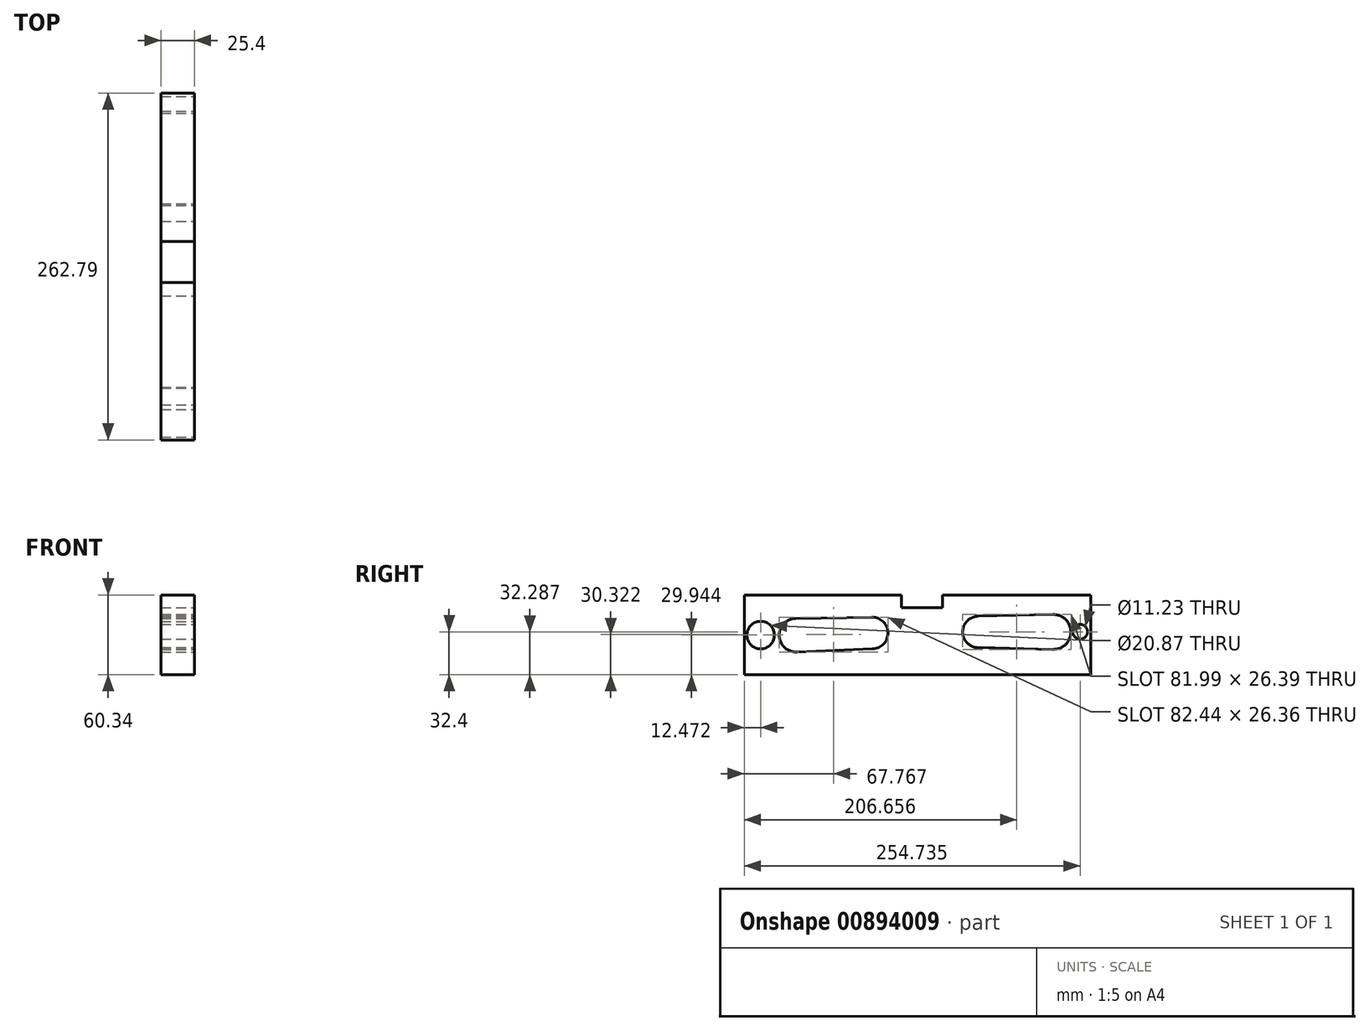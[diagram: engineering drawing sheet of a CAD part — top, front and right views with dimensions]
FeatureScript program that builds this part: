
annotation { "Feature Type Name" : "Feature", "Feature Type Description" : "" }
export const myFeature = defineFeature(function(context is Context, id is Id, definition is map)
    precondition{}
    {
        {
            var Q0;
            Q0=qCreatedBy(makeId("Right.planeOp"),FACE);
            var sketch = newSketch(context, id + "F0", { "sketchPlane" : qUnion([Q0])});
            skLineSegment(sketch, "E0", {"start": v(-89.26, -13.23) * mm, "end": v(-89.26, -73.57) * mm});
            skLineSegment(sketch, "E1", {"start": v(-89.26, -73.57) * mm, "end": v(173.53, -73.57) * mm});
            skLineSegment(sketch, "E2", {"start": v(173.53, -73.57) * mm, "end": v(173.53, -13.23) * mm});
            skLineSegment(sketch, "E3", {"start": v(173.53, -13.23) * mm, "end": v(-89.26, -13.23) * mm});
            skSolve(sketch);
        }
        {
            var Q0;
            Q0 = qSketchRegion(id + "F0", true);
            extrude(context, id + "F1", {"entities" : qUnion([Q0]), "depth" : 25.4 * mm, "offsetDistance" : 25.4 * mm});
        }
        {
            var Q0;
            Q0=makeQuery(id+"F1.opExtrude","CAP_FACE",FACE,{"disambiguationData":[OSD([sQuery(id+"F0.wireOp",EDGE,"E0"),sQuery(id+"F0.wireOp",EDGE,"E1"),sQuery(id+"F0.wireOp",EDGE,"E2"),sQuery(id+"F0.wireOp",EDGE,"E3")])],"isStart":false});
            var sketch = newSketch(context, id + "F2", { "sketchPlane" : qUnion([Q0])});
            skArc(sketch, "E4", {"start": v(-50, -31.03) * mm, "mid": v(-62.71, -44.12) * mm, "end": v(-49.24, -56.43) * mm});
            skArc(sketch, "E5", {"start": v(8.18, -54.13) * mm, "mid": v(19.73, -41.76) * mm, "end": v(7.5, -30.07) * mm});
            skArc(sketch, "E6", {"start": v(88.31, -29.35) * mm, "mid": v(76.4, -41.92) * mm, "end": v(89.6, -53.14) * mm});
            skArc(sketch, "E7", {"start": v(144.88, -54.48) * mm, "mid": v(158.4, -41.3) * mm, "end": v(144.9, -28.09) * mm});
            skLineSegment(sketch, "E8", {"start": v(-50, -31.03) * mm, "end": v(7.5, -30.07) * mm});
            skLineSegment(sketch, "E9", {"start": v(-49.24, -56.43) * mm, "end": v(8.18, -54.13) * mm});
            skLineSegment(sketch, "E10", {"start": v(89.6, -53.14) * mm, "end": v(144.88, -54.48) * mm});
            skLineSegment(sketch, "E11", {"start": v(88.31, -29.35) * mm, "end": v(144.9, -28.09) * mm});
            skSolve(sketch);
        }
        {
            var Q0;
            Q0 = qSketchRegion(id + "F2", true);
            extrude(context, id + "F3", {"entities" : qUnion([Q0]), "operationType" : NewBodyOperationType.REMOVE, "oppositeDirection" : true, "depth" : 25.4 * mm, "offsetDistance" : 25.4 * mm});
        }
        {
            var Q0;
            Q0=makeQuery(id+"F1.opExtrude","CAP_FACE",FACE,{"disambiguationData":[OSD([sQuery(id+"F0.wireOp",EDGE,"E0"),sQuery(id+"F0.wireOp",EDGE,"E1"),sQuery(id+"F0.wireOp",EDGE,"E2"),sQuery(id+"F0.wireOp",EDGE,"E3")])],"isStart":false});
            var sketch = newSketch(context, id + "F4", { "sketchPlane" : qUnion([Q0])});
            skLineSegment(sketch, "E12", {"start": v(30.1, -13.23) * mm, "end": v(30.1, -22.8) * mm});
            skLineSegment(sketch, "E13", {"start": v(30.1, -22.8) * mm, "end": v(61.07, -22.8) * mm});
            skLineSegment(sketch, "E14", {"start": v(61.07, -22.8) * mm, "end": v(61.07, -13.23) * mm});
            skLineSegment(sketch, "E15", {"start": v(30.1, -13.23) * mm, "end": v(61.07, -13.23) * mm});
            skSolve(sketch);
        }
        {
            var Q0;
            Q0 = qSketchRegion(id + "F4", true);
            extrude(context, id + "F5", {"entities" : qUnion([Q0]), "operationType" : NewBodyOperationType.REMOVE, "oppositeDirection" : true, "depth" : 25.4 * mm, "offsetDistance" : 25.4 * mm});
        }
        {
            var Q0;
            Q0=makeQuery(id+"F1.opExtrude","CAP_FACE",FACE,{"disambiguationData":[OSD([sQuery(id+"F0.wireOp",EDGE,"E0"),sQuery(id+"F0.wireOp",EDGE,"E1"),sQuery(id+"F0.wireOp",EDGE,"E2"),sQuery(id+"F0.wireOp",EDGE,"E3")])],"isStart":false});
            var sketch = newSketch(context, id + "F6", { "sketchPlane" : qUnion([Q0])});
            skCircle(sketch, "E16", {"center": v(-76.79, -43.63) * mm, "radius": 10.43 * mm});
            skCircle(sketch, "E17", {"center": v(165.47, -41.17) * mm, "radius": 5.62 * mm});
            skSolve(sketch);
        }
        {
            var Q0;
            Q0 = qSketchRegion(id + "F6", true);
            extrude(context, id + "F7", {"entities" : qUnion([Q0]), "operationType" : NewBodyOperationType.REMOVE, "oppositeDirection" : true, "depth" : 25.4 * mm, "offsetDistance" : 25.4 * mm});
        }
    });
